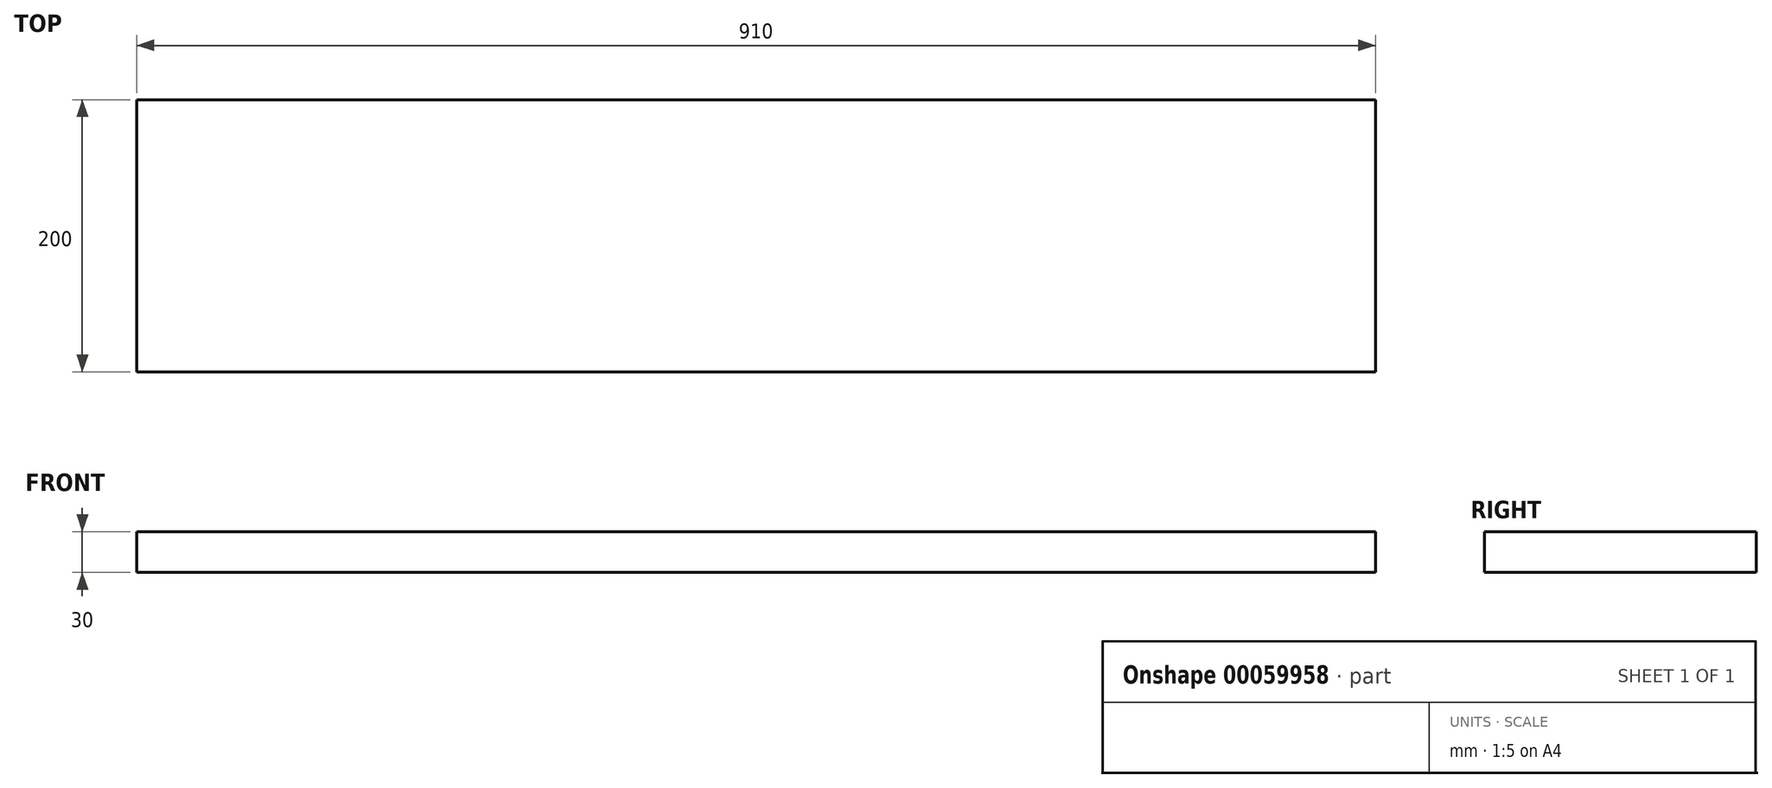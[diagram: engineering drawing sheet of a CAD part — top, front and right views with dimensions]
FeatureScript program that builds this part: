
annotation { "Feature Type Name" : "Feature", "Feature Type Description" : "" }
export const myFeature = defineFeature(function(context is Context, id is Id, definition is map)
    precondition{}
    {
        {
            var Q0;
            Q0=qCreatedBy(makeId("Top.planeOp"),FACE);
            var sketch = newSketch(context, id + "F0", { "sketchPlane" : qUnion([Q0])});
            skLineSegment(sketch, "E0.rect.bottom", {"start": v(455, -100) * mm, "end": v(-455, -100) * mm});
            skLineSegment(sketch, "E0.rect.top", {"start": v(455, 100) * mm, "end": v(-455, 100) * mm});
            skLineSegment(sketch, "E0.rect.left", {"start": v(455, -100) * mm, "end": v(455, 100) * mm});
            skLineSegment(sketch, "E0.rect.right", {"start": v(-455, -100) * mm, "end": v(-455, 100) * mm});
            skPoint(sketch, "E0.rect.middle", {"position": v(0, 0) * mm});
            skSolve(sketch);
        }
        {
            var Q0;
            Q0=makeQuery(id+"F0.imprint","IMPRINT",FACE,{"disambiguationData":[TD([[makeQuery(id+"F0.imprint","IMPRINT",EDGE,{"derivedFrom":sQuery(id+"F0.wireOp",EDGE,"E0.rect.bottom")}),-1.0]])]});
            extrude(context, id + "F1", {"entities" : qUnion([Q0]), "oppositeDirection" : true, "depth" : 30 * mm});
        }
    });
